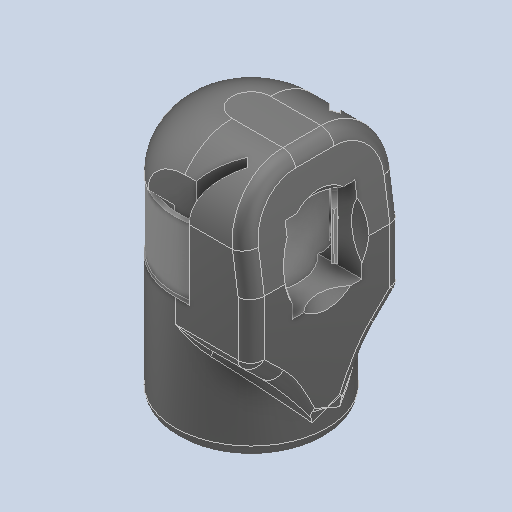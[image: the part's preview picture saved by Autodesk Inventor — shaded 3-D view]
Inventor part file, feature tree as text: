
AUTODESK INVENTOR PART (.ipt)
format: ipt  version: 2024 (Build 280153000, 153)  size: 375,296 bytes
history: native  units: mm
features: other x3, fillet x1
ambient origin geometry x8: Origin, YZ Plane, XZ Plane, XY Plane, X Axis, Y Axis, Z Axis, Center Point
bodies: Solid1 (feature_tree), Solid2 (feature_tree)
feature tree (4):
  other  "Plane1"
  other  "Plane2"
  fillet  "Fillet10"  [1 undecoded]
  other  "Cut-Extrude6"
note: 1 required parameter value undecoded (feature->parameter linkage not recoverable at this tier; creation-order binding heuristic only, values carry confidence <= 0.55)
